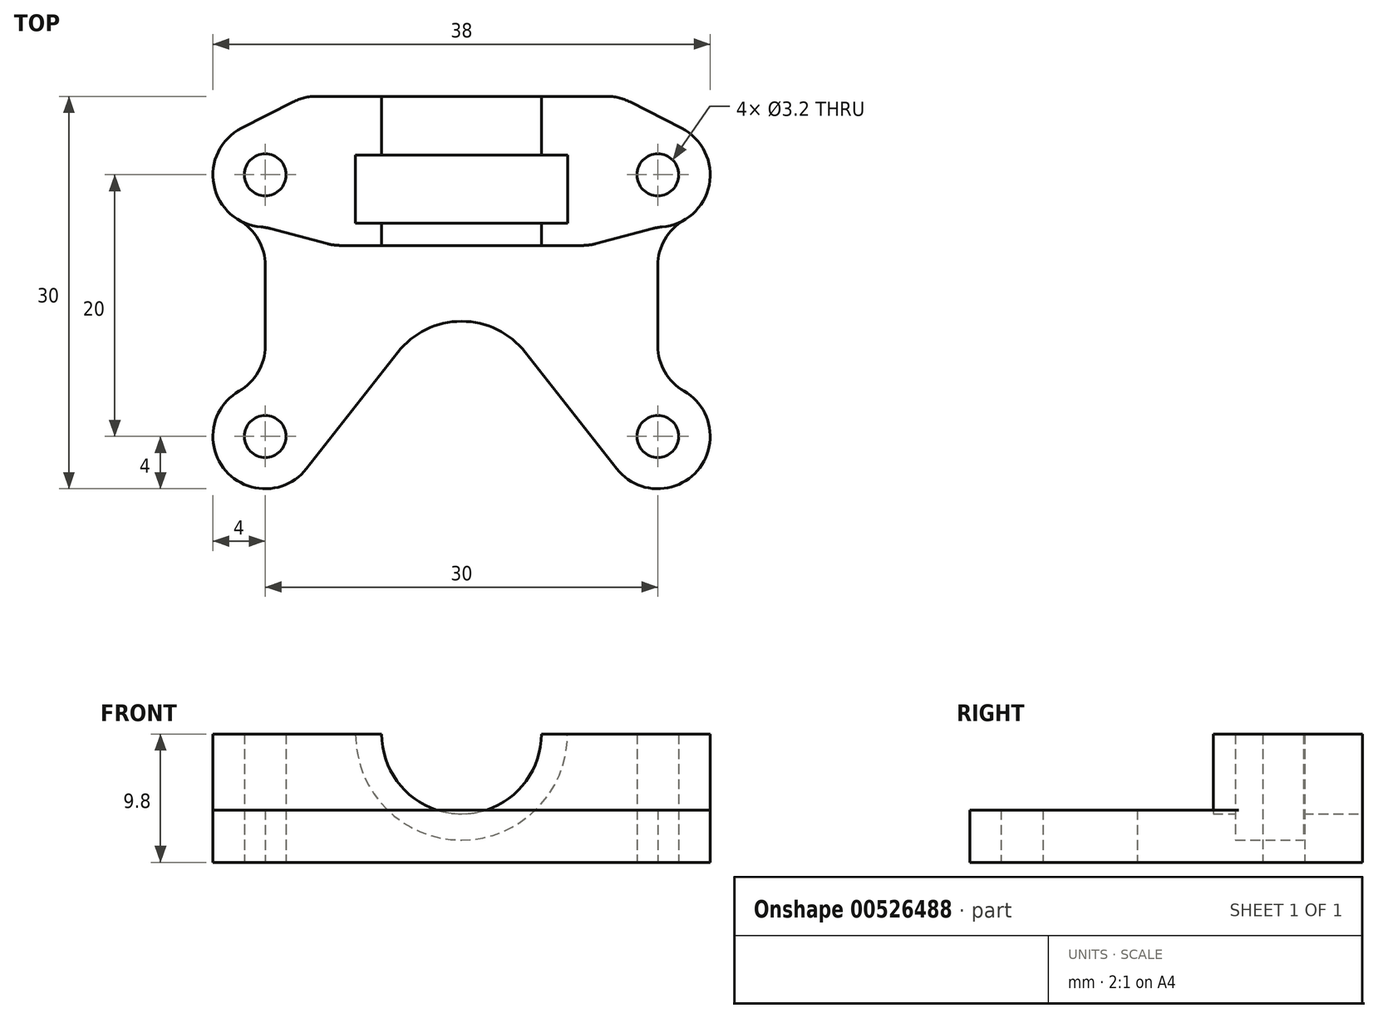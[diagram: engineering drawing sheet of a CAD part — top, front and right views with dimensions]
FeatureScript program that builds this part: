
annotation { "Feature Type Name" : "Feature", "Feature Type Description" : "" }
export const myFeature = defineFeature(function(context is Context, id is Id, definition is map)
    precondition{}
    {
        {
            var Q0;
            Q0=qCreatedBy(makeId("Top.planeOp"),FACE);
            var sketch = newSketch(context, id + "F0", { "sketchPlane" : qUnion([Q0])});
            skCircle(sketch, "E0", {"center": v(-15, 0) * mm, "radius": 1.6 * mm});
            skLineSegment(sketch, "E1", {"start": v(0, 6) * mm, "end": v(-12.04, 6) * mm});
            skLineSegment(sketch, "E2", {"start": v(-16.82, 3.56) * mm, "end": v(-12.04, 6) * mm});
            skLineSegment(sketch, "E3", {"start": v(-15, -4) * mm, "end": v(-9.78, -5.4) * mm});
            skLineSegment(sketch, "E4", {"start": v(-9.78, -5.4) * mm, "end": v(0, -5.4) * mm});
            skLineSegment(sketch, "E5", {"start": v(0, -5.4) * mm, "end": v(0, 6) * mm});
            skArc(sketch, "E6", {"start": v(-16.82, 3.56) * mm, "mid": v(-18.89, -0.93) * mm, "end": v(-15, -4) * mm});
            skSolve(sketch);
        }
        {
            var Q0;
            Q0=qSketchRegion(id+"F0",true);
            extrude(context, id + "F1", {"entities" : qUnion([Q0]), "depth" : 9.8 * mm, "offsetDistance" : 25 * mm});
        }
        {
            var Q0;
            Q0=makeQuery(id+"F1.opExtrude","CAP_FACE",FACE,{"disambiguationData":[OSD([sQuery(id+"F0.wireOp",EDGE,"E0"),sQuery(id+"F0.wireOp",EDGE,"E1"),sQuery(id+"F0.wireOp",EDGE,"E2"),sQuery(id+"F0.wireOp",EDGE,"E3"),sQuery(id+"F0.wireOp",EDGE,"E4"),sQuery(id+"F0.wireOp",EDGE,"E5"),sQuery(id+"F0.wireOp",EDGE,"E6")])],"isStart":false});
            var sketch = newSketch(context, id + "F2", { "sketchPlane" : qUnion([Q0])});
            skLineSegment(sketch, "E7", {"start": v(0, 6) * mm, "end": v(-6.1, 6) * mm});
            skLineSegment(sketch, "E8", {"start": v(-6.1, 6) * mm, "end": v(-6.1, 1.5) * mm});
            skLineSegment(sketch, "E9", {"start": v(-6.1, 1.5) * mm, "end": v(-8.1, 1.5) * mm});
            skLineSegment(sketch, "E10", {"start": v(-8.1, 1.5) * mm, "end": v(-8.1, -3.7) * mm});
            skLineSegment(sketch, "E11", {"start": v(-8.1, -3.7) * mm, "end": v(-6.1, -3.7) * mm});
            skLineSegment(sketch, "E12", {"start": v(-6.1, -3.7) * mm, "end": v(-6.1, -5.4) * mm});
            skLineSegment(sketch, "E13", {"start": v(-6.1, -5.4) * mm, "end": v(0, -5.4) * mm});
            skLineSegment(sketch, "E14", {"start": v(0, -5.4) * mm, "end": v(0, 6) * mm});
            skSolve(sketch);
        }
        {
            var Q0;
            Q0=qSketchRegion(id+"F2",true);
            var Q1;
            Q1=sQuery(id+"F2.wireOp",EDGE,"E14");
            revolve(context, id + "F3", {"operationType" : NewBodyOperationType.REMOVE, "entities" : qUnion([Q0]), "axis" : qUnion([Q1]), "revolveType" : RevolveType.FULL, "oppositeDirection" : true});
        }
        {
            var Q0;
            Q0=makeQuery(id+"F1.opExtrude","SWEPT_EDGE",EDGE,{"disambiguationData":[OSD([sQuery(id+"F0.wireOp",EDGE,"E3"),sQuery(id+"F0.wireOp",EDGE,"E6")])]});
            var Q1;
            Q1=makeQuery(id+"F1.opExtrude","SWEPT_EDGE",EDGE,{"disambiguationData":[OSD([sQuery(id+"F0.wireOp",EDGE,"E3"),sQuery(id+"F0.wireOp",EDGE,"E4")])]});
            var Q2;
            Q2=makeQuery(id+"F1.opExtrude","SWEPT_EDGE",EDGE,{"disambiguationData":[OSD([sQuery(id+"F0.wireOp",EDGE,"E1"),sQuery(id+"F0.wireOp",EDGE,"E2")])]});
            var Q3;
            Q3=makeQuery(id+"F1.opExtrude","SWEPT_EDGE",EDGE,{"disambiguationData":[OSD([sQuery(id+"F0.wireOp",EDGE,"E2"),sQuery(id+"F0.wireOp",EDGE,"E6")])]});
            fillet(context, id + "F4", {"entities" : qUnion([Q0, Q1, Q2, Q3]), "radius" : 4 * mm, "tangentPropagation" : true, "allowEdgeOverflow" : false});
        }
        {
            var Q0;
            Q0=makeQuery(id+"F1.opExtrude","CAP_FACE",FACE,{"disambiguationData":[OSD([sQuery(id+"F0.wireOp",EDGE,"E0"),sQuery(id+"F0.wireOp",EDGE,"E1"),sQuery(id+"F0.wireOp",EDGE,"E2"),sQuery(id+"F0.wireOp",EDGE,"E3"),sQuery(id+"F0.wireOp",EDGE,"E4"),sQuery(id+"F0.wireOp",EDGE,"E5"),sQuery(id+"F0.wireOp",EDGE,"E6")])],"isStart":true});
            var sketch = newSketch(context, id + "F5", { "sketchPlane" : qUnion([Q0])});
            skPoint(sketch, "E15", {"position": v(-15, 0) * mm});
            skLineSegment(sketch, "E16", {"start": v(0, 5.4) * mm, "end": v(0, 11.2) * mm});
            skArc(sketch, "E17", {"start": v(0, 11.2) * mm, "mid": v(-2.71, 11.83) * mm, "end": v(-4.88, 13.57) * mm});
            skCircle(sketch, "E18", {"center": v(-15, 20) * mm, "radius": 1.6 * mm});
            skArc(sketch, "E19", {"start": v(-17, 16.54) * mm, "mid": v(-18.02, 22.62) * mm, "end": v(-11.85, 22.47) * mm});
            skLineSegment(sketch, "E20", {"start": v(-11.85, 22.47) * mm, "end": v(-4.88, 13.57) * mm});
            skArc(sketch, "E21", {"start": v(-17, 16.54) * mm, "mid": v(-15.54, 15.07) * mm, "end": v(-15, 13.07) * mm});
            skLineSegment(sketch, "E22", {"start": v(-15, 13.07) * mm, "end": v(-15, 6.93) * mm});
            skArc(sketch, "E23", {"start": v(-15, 6.93) * mm, "mid": v(-15.54, 4.93) * mm, "end": v(-17, 3.46) * mm});
            skArc(sketch, "E24.0", {"start": v(-15.3, 3.99) * mm, "mid": v(-14.94, 4.03) * mm, "end": v(-14.58, 4.11) * mm});
            skLineSegment(sketch, "E25.0", {"start": v(-14.58, 4.11) * mm, "end": v(-10.28, 5.26) * mm});
            skArc(sketch, "E26.0", {"start": v(-10.28, 5.26) * mm, "mid": v(-9.77, 5.37) * mm, "end": v(-9.25, 5.4) * mm});
            skLineSegment(sketch, "E27.0", {"start": v(-9.25, 5.4) * mm, "end": v(-6.1, 5.4) * mm});
            skLineSegment(sketch, "E28.0", {"start": v(0, 5.4) * mm, "end": v(-6.1, 5.4) * mm});
            skSolve(sketch);
        }
        {
            var Q0;
            Q0=makeQuery(id+"F5.imprint","IMPRINT",FACE,{"disambiguationData":[TD([[makeQuery(id+"F5.imprint","IMPRINT",EDGE,{"derivedFrom":sQuery(id+"F5.wireOp",EDGE,"E16")}),1.0]])]});
            extrude(context, id + "F6", {"entities" : qUnion([Q0]), "operationType" : NewBodyOperationType.ADD, "oppositeDirection" : true, "depth" : 4 * mm, "offsetDistance" : 25 * mm});
        }
        {
            var Q0;
            Q0=makeQuery(id+"F1.opExtrude","SWEPT_BODY",BODY,{"disambiguationData":[OSD([sQuery(id+"F0.wireOp",EDGE,"E0"),sQuery(id+"F0.wireOp",EDGE,"E1"),sQuery(id+"F0.wireOp",EDGE,"E2"),sQuery(id+"F0.wireOp",EDGE,"E3"),sQuery(id+"F0.wireOp",EDGE,"E4"),sQuery(id+"F0.wireOp",EDGE,"E5"),sQuery(id+"F0.wireOp",EDGE,"E6")])]});
            var Q1;
            Q1=makeQuery(id+"F6.boolean.opBoolean","MERGE",FACE,{"derivedFrom":[makeQuery(id+"F1.opExtrude","SWEPT_FACE",FACE,{"disambiguationData":[OSD([sQuery(id+"F0.wireOp",EDGE,"E5")])]}),makeQuery(id+"F6.opExtrude","SWEPT_FACE",FACE,{"disambiguationData":[OSD([sQuery(id+"F5.wireOp",EDGE,"LbYneBzx-AH3K-77wf-vux2-KZwJ9vFJ22zI")])]})]});
            mirror(context, id + "F7", {"operationType" : NewBodyOperationType.ADD, "entities" : qUnion([Q0]), "mirrorPlane" : qUnion([Q1])});
        }
    });
